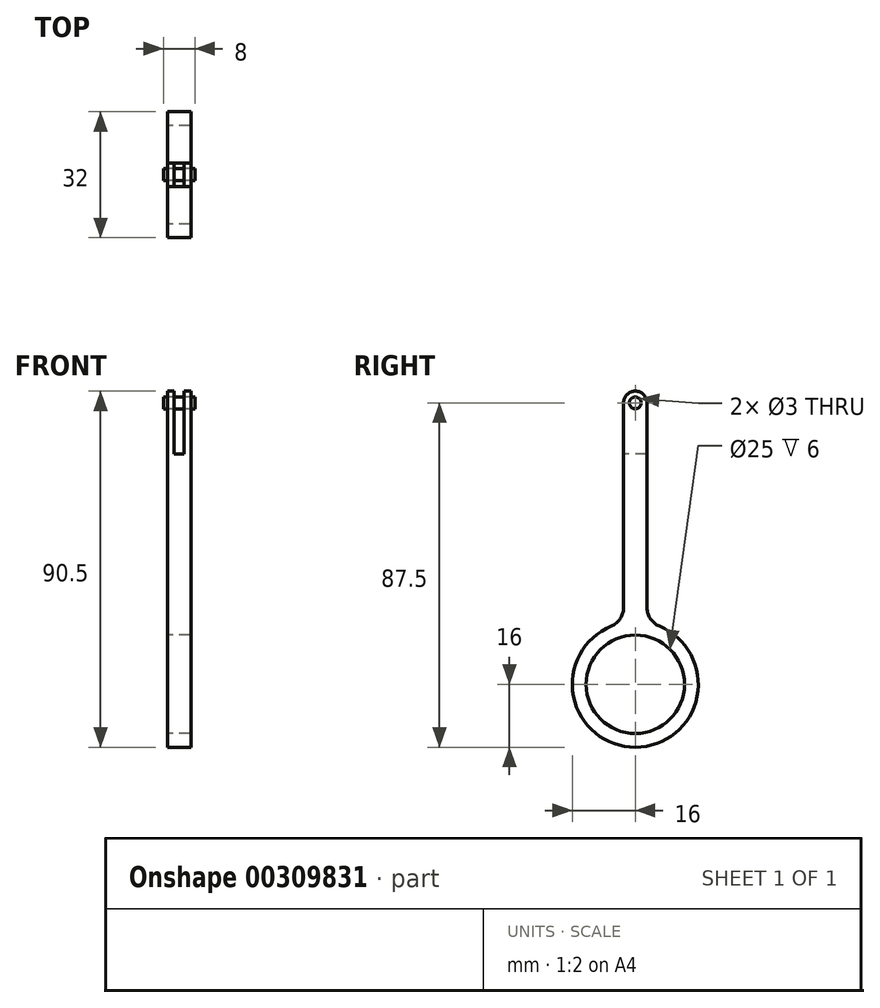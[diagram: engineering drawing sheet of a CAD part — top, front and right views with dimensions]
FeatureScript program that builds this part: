
annotation { "Feature Type Name" : "Feature", "Feature Type Description" : "" }
export const myFeature = defineFeature(function(context is Context, id is Id, definition is map)
    precondition{}
    {
        {
            var Q0;
            Q0=qCreatedBy(makeId("Right.planeOp"),FACE);
            var sketch = newSketch(context, id + "F0", { "sketchPlane" : qUnion([Q0])});
            skCircle(sketch, "E0", {"center": v(0, 0) * mm, "radius": 12.5 * mm});
            skArc(sketch, "E1", {"start": v(-6.1, 14.8) * mm, "mid": v(0, -16) * mm, "end": v(6.1, 14.8) * mm});
            skLineSegment(sketch, "E2", {"start": v(0, -27.87) * mm, "end": v(0, 67.37) * mm, "construction": true});
            skLineSegment(sketch, "E3", {"start": v(-3, 71.5) * mm, "end": v(-3, 19.42) * mm});
            skLineSegment(sketch, "E4", {"start": v(3, 19.42) * mm, "end": v(3, 71.5) * mm});
            skArc(sketch, "E5", {"start": v(-3, 71.5) * mm, "mid": v(0, 74.5) * mm, "end": v(3, 71.5) * mm});
            skCircle(sketch, "E6", {"center": v(0, 71.5) * mm, "radius": 1.5 * mm});
            skArc(sketch, "E7", {"start": v(-3, 19.42) * mm, "mid": v(-3.85, 16.63) * mm, "end": v(-6.1, 14.8) * mm});
            skArc(sketch, "E8", {"start": v(3, 19.42) * mm, "mid": v(3.85, 16.63) * mm, "end": v(6.1, 14.8) * mm});
            skSolve(sketch);
        }
        {
            var Q0;
            Q0 = qSketchRegion(id + "F0", true);
            extrude(context, id + "F1", {"entities" : qUnion([Q0]), "depth" : 6 * mm});
        }
        {
            var Q0;
            Q0=makeQuery(id+"F1.opExtrude","SWEPT_FACE",FACE,{"disambiguationData":[OSD([sQuery(id+"F0.wireOp",EDGE,"E3")])]});
            var sketch = newSketch(context, id + "F2", { "sketchPlane" : qUnion([Q0])});
            skLineSegment(sketch, "E9.bottom", {"start": v(1.75, 58.5) * mm, "end": v(4.25, 58.5) * mm});
            skLineSegment(sketch, "E9.top", {"start": v(1.75, 77.5) * mm, "end": v(4.25, 77.5) * mm});
            skLineSegment(sketch, "E9.left", {"start": v(1.75, 58.5) * mm, "end": v(1.75, 77.5) * mm});
            skLineSegment(sketch, "E9.right", {"start": v(4.25, 58.5) * mm, "end": v(4.25, 77.5) * mm});
            skLineSegment(sketch, "E10", {"start": v(3, 54.97) * mm, "end": v(3, 81.27) * mm, "construction": true});
            skPoint(sketch, "E10.startSnap0", {"position": v(3, 71.5) * mm});
            skSolve(sketch);
        }
        {
            var Q0;
            {var subQ0=sQuery(id+"F2.wireOp",EDGE,"E9.top");Q0=makeQuery(id+"F2.imprint","IMPRINT",FACE,{"disambiguationData":[TD([[makeQuery(id+"F2.imprint","IMPRINT",EDGE,{"derivedFrom":subQ0}),-1.0]])]});}
            var Q1;
            {var subQ0=sQuery(id+"F2.wireOp",EDGE,"E9.bottom");Q1=makeQuery(id+"F2.imprint","IMPRINT",FACE,{"disambiguationData":[TD([[makeQuery(id+"F2.imprint","IMPRINT",EDGE,{"derivedFrom":subQ0}),1.0]])]});}
            extrude(context, id + "F3", {"entities" : qUnion([Q0, Q1]), "operationType" : NewBodyOperationType.REMOVE, "endBound" : BoundingType.THROUGH_ALL, "oppositeDirection" : true, "depth" : 25 * mm});
        }
        {
            var Q0;
            Q0=makeQuery(id+"F1.opExtrude","CAP_FACE",FACE,{"disambiguationData":[OSD([sQuery(id+"F0.wireOp",EDGE,"E0"),sQuery(id+"F0.wireOp",EDGE,"E1"),sQuery(id+"F0.wireOp",EDGE,"E3"),sQuery(id+"F0.wireOp",EDGE,"E4"),sQuery(id+"F0.wireOp",EDGE,"E5"),sQuery(id+"F0.wireOp",EDGE,"E6"),sQuery(id+"F0.wireOp",EDGE,"E7"),sQuery(id+"F0.wireOp",EDGE,"E8")])],"isStart":false});
            var sketch = newSketch(context, id + "F4", { "sketchPlane" : qUnion([Q0])});
            skCircle(sketch, "E11", {"center": v(0, 71.5) * mm, "radius": 1.5 * mm});
            skSolve(sketch);
        }
        {
            var Q0;
            Q0=makeQuery(id+"F4.imprint","IMPRINT",FACE,{"disambiguationData":[TD([[makeQuery(id+"F4.imprint","IMPRINT",EDGE,{"derivedFrom":sQuery(id+"F4.wireOp",EDGE,"E11")}),1.0]])]});
            extrude(context, id + "F5", {"entities" : qUnion([Q0]), "depth" : 1 * mm, "hasSecondDirection" : true, "secondDirectionOppositeDirection" : true, "secondDirectionDepth" : 7 * mm});
        }
    });
